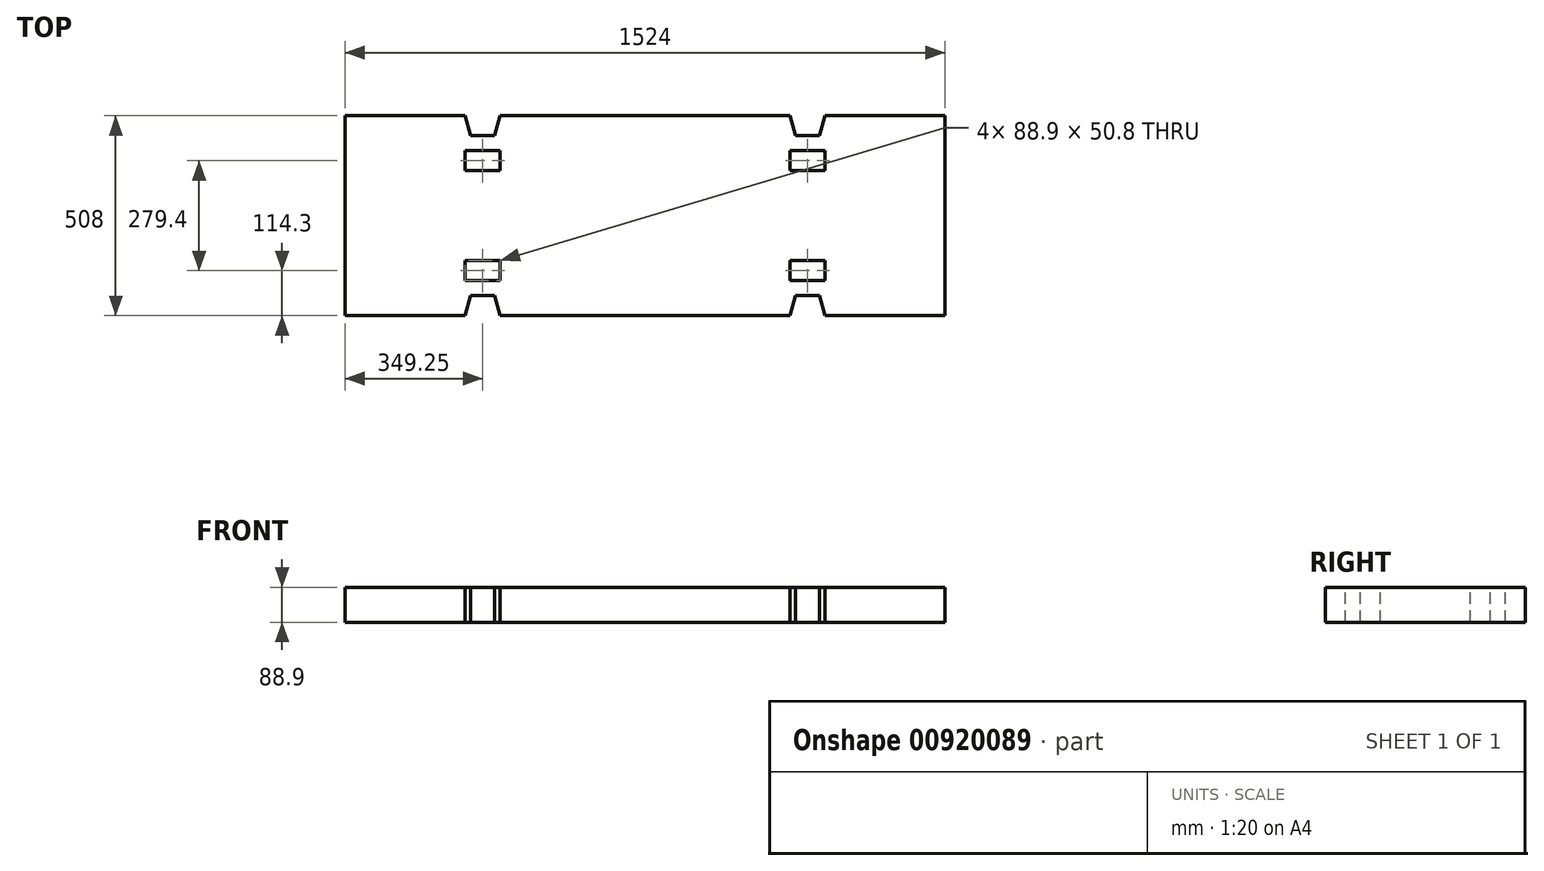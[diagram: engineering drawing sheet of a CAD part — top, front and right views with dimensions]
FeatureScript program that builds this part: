
annotation { "Feature Type Name" : "Feature", "Feature Type Description" : "" }
export const myFeature = defineFeature(function(context is Context, id is Id, definition is map)
    precondition{}
    {
        {
            var Q0;
            Q0=qCreatedBy(makeId("Top.planeOp"),FACE);
            var sketch = newSketch(context, id + "F0", { "sketchPlane" : qUnion([Q0])});
            skLineSegment(sketch, "E0.bottom", {"start": v(0, 0) * mm, "end": v(1524, 0) * mm});
            skLineSegment(sketch, "E0.top", {"start": v(0, 508) * mm, "end": v(1524, 508) * mm});
            skLineSegment(sketch, "E0.left", {"start": v(0, 0) * mm, "end": v(0, 508) * mm});
            skLineSegment(sketch, "E0.right", {"start": v(1524, 0) * mm, "end": v(1524, 508) * mm});
            skSolve(sketch);
        }
        {
            var Q0;
            Q0=makeQuery(id+"F0.imprint","IMPRINT",FACE,{"disambiguationData":[TD([[makeQuery(id+"F0.imprint","IMPRINT",EDGE,{"derivedFrom":sQuery(id+"F0.wireOp",EDGE,"E0.bottom")}),1.0]])]});
            extrude(context, id + "F1", {"entities" : qUnion([Q0]), "depth" : 88.9 * mm, "offsetDistance" : 25.4 * mm});
        }
        {
            var Q0;
            Q0=makeQuery(id+"F1.opExtrude","CAP_FACE",FACE,{"disambiguationData":[OSD([sQuery(id+"F0.wireOp",EDGE,"E0.bottom"),sQuery(id+"F0.wireOp",EDGE,"E0.top"),sQuery(id+"F0.wireOp",EDGE,"E0.left"),sQuery(id+"F0.wireOp",EDGE,"E0.right")])],"isStart":false});
            var sketch = newSketch(context, id + "F2", { "sketchPlane" : qUnion([Q0])});
            skLineSegment(sketch, "E1", {"start": v(304.8, 0) * mm, "end": v(393.7, 0) * mm});
            skLineSegment(sketch, "E2", {"start": v(393.7, 0) * mm, "end": v(380.09, 50.8) * mm});
            skLineSegment(sketch, "E3", {"start": v(380.09, 50.8) * mm, "end": v(318.41, 50.8) * mm});
            skLineSegment(sketch, "E4", {"start": v(318.41, 50.8) * mm, "end": v(304.8, 0) * mm});
            skLineSegment(sketch, "E5", {"start": v(304.8, 88.9) * mm, "end": v(393.7, 88.9) * mm});
            skLineSegment(sketch, "E6", {"start": v(393.7, 88.9) * mm, "end": v(393.7, 139.7) * mm});
            skLineSegment(sketch, "E7", {"start": v(393.7, 139.7) * mm, "end": v(304.8, 139.7) * mm});
            skLineSegment(sketch, "E8", {"start": v(304.8, 139.7) * mm, "end": v(304.8, 88.9) * mm});
            skLineSegment(sketch, "E9", {"start": v(1130.3, 0) * mm, "end": v(1219.2, 0) * mm});
            skLineSegment(sketch, "E10", {"start": v(1219.2, 0) * mm, "end": v(1205.59, 50.8) * mm});
            skLineSegment(sketch, "E11", {"start": v(1205.59, 50.8) * mm, "end": v(1143.91, 50.8) * mm});
            skLineSegment(sketch, "E12", {"start": v(1143.91, 50.8) * mm, "end": v(1130.3, 0) * mm});
            skLineSegment(sketch, "E13", {"start": v(1130.3, 88.9) * mm, "end": v(1219.2, 88.9) * mm});
            skLineSegment(sketch, "E14", {"start": v(1219.2, 88.9) * mm, "end": v(1219.2, 139.7) * mm});
            skLineSegment(sketch, "E15", {"start": v(1219.2, 139.7) * mm, "end": v(1130.3, 139.7) * mm});
            skLineSegment(sketch, "E16", {"start": v(1130.3, 139.7) * mm, "end": v(1130.3, 88.9) * mm});
            skLineSegment(sketch, "E17", {"start": v(1524, 254) * mm, "end": v(0, 254) * mm, "construction": true});
            skLineSegment(sketch, "E18.MirrorCS", {"start": v(380.09, 457.2) * mm, "end": v(318.41, 457.2) * mm});
            skLineSegment(sketch, "E19.MirrorCS", {"start": v(318.41, 457.2) * mm, "end": v(304.8, 508) * mm});
            skLineSegment(sketch, "E20.MirrorCS", {"start": v(1219.2, 419.1) * mm, "end": v(1219.2, 368.3) * mm});
            skLineSegment(sketch, "E21.MirrorCS", {"start": v(393.7, 419.1) * mm, "end": v(393.7, 368.3) * mm});
            skLineSegment(sketch, "E22.MirrorCS", {"start": v(393.7, 508) * mm, "end": v(380.09, 457.2) * mm});
            skLineSegment(sketch, "E23.MirrorCS", {"start": v(304.8, 368.3) * mm, "end": v(304.8, 419.1) * mm});
            skLineSegment(sketch, "E24.MirrorCS", {"start": v(1219.2, 508) * mm, "end": v(1205.59, 457.2) * mm});
            skLineSegment(sketch, "E25.MirrorCS", {"start": v(1143.91, 457.2) * mm, "end": v(1130.3, 508) * mm});
            skLineSegment(sketch, "E26.MirrorCS", {"start": v(1130.3, 368.3) * mm, "end": v(1130.3, 419.1) * mm});
            skLineSegment(sketch, "E27.MirrorCS", {"start": v(1205.59, 457.2) * mm, "end": v(1143.91, 457.2) * mm});
            skLineSegment(sketch, "E28.MirrorCS", {"start": v(1130.3, 508) * mm, "end": v(1219.2, 508) * mm});
            skLineSegment(sketch, "E29.MirrorCS", {"start": v(304.8, 508) * mm, "end": v(393.7, 508) * mm});
            skLineSegment(sketch, "E30.MirrorCS", {"start": v(1219.2, 368.3) * mm, "end": v(1130.3, 368.3) * mm});
            skLineSegment(sketch, "E31.MirrorCS", {"start": v(304.8, 419.1) * mm, "end": v(393.7, 419.1) * mm});
            skLineSegment(sketch, "E32.MirrorCS", {"start": v(1130.3, 419.1) * mm, "end": v(1219.2, 419.1) * mm});
            skLineSegment(sketch, "E33.MirrorCS", {"start": v(393.7, 368.3) * mm, "end": v(304.8, 368.3) * mm});
            skSolve(sketch);
        }
        {
            var Q0;
            Q0 = qSketchRegion(id + "F2", true);
            extrude(context, id + "F3", {"entities" : qUnion([Q0]), "operationType" : NewBodyOperationType.REMOVE, "endBound" : BoundingType.UP_TO_NEXT, "oppositeDirection" : true, "depth" : 25.4 * mm, "offsetDistance" : 25.4 * mm});
        }
    });
